# Revit family: Toilet_Seat-Elongated_Cleansing-KOHLER-C3_050-K-18751
name_source: partatom
category: Specialty Equipment
revit_build: Autodesk Revit 2015 (Build: 20140606_1530(x64)
units: mm (PartAtom-declared; Revit-internal decimal feet)

## types (2) — shared parameters
ADA Compliant = No
Apparent Load = 1800 VA
Assembly Code = C1030200
CW Connection = Yes
Cold Water Inlet = Cold Water Inlet
Date Modified = 12/07/2018
Default Elevation = 0"
Description = Cleansing toilet seat, elongated
Electrical Connector = Yes
Electrical Note = One dedicated circuit required, protected with Class A Ground-Fault Circuit-Interrupter (GFCI) or Residual Current Device (RCD)
Height = 4 3/4"
Length = 20 11/16"
Manufacturer = KOHLER Co.
MasterFormat 1995 = 10820
MasterFormat 2004 = 10.28.13
Material = Polypropylene Plastic
Product Documentation Link = http://www.us.kohler.com
Product Name = C3-050
Product Page URL = http://www.us.kohler.com
URL = https://www.us.kohler.com
Voltage = 120 V
Width = 16 15/16"

## per-type parameters (varying)
| type | Finish | Model | Type |
| 0-White | Kohler-Plastic-0-White | K-18751-0 | 1 |
| 96-Biscuit | Kohler-Plastic-96-Biscuit | K-18751-96 | 2 |

## geometry (parser evidence)
native form markers: Sweep x5
no freeform markers — native parametric forms only
